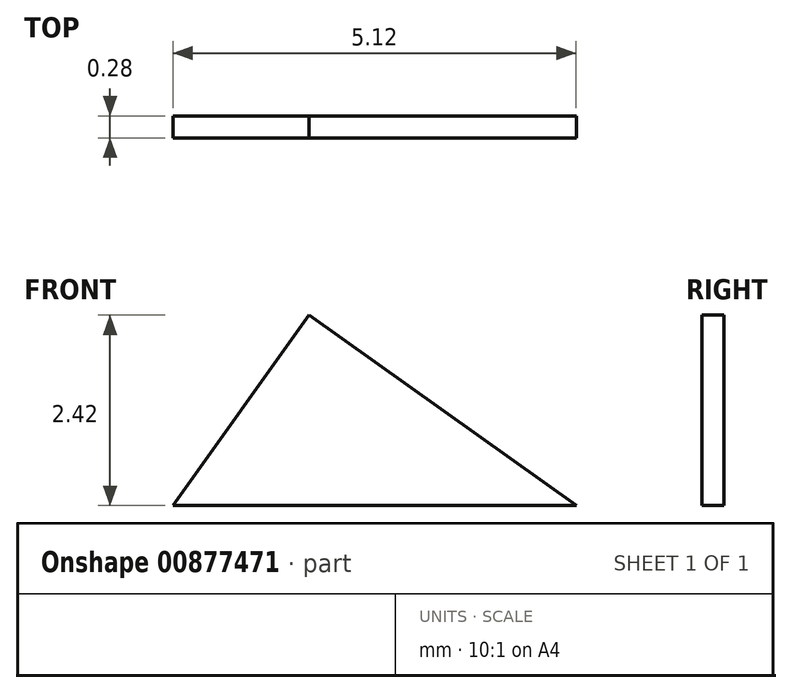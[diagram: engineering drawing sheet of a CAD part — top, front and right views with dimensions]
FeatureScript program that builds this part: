
annotation { "Feature Type Name" : "Feature", "Feature Type Description" : "" }
export const myFeature = defineFeature(function(context is Context, id is Id, definition is map)
    precondition{}
    {
        {
            var Q0;
            Q0=qCreatedBy(makeId("Front.planeOp"),FACE);
            var sketch = newSketch(context, id + "F0", { "sketchPlane" : qUnion([Q0])});
            skLineSegment(sketch, "E0", {"start": v(-6.23, 0) * mm, "end": v(-1.1, 0) * mm});
            skLineSegment(sketch, "E1", {"start": v(-1.1, 0) * mm, "end": v(-4.5, 2.42) * mm});
            skLineSegment(sketch, "E2", {"start": v(-4.5, 2.42) * mm, "end": v(-6.23, 0) * mm});
            skSolve(sketch);
        }
        {
            var Q0;
            Q0=makeQuery(id+"F0.imprint","IMPRINT",FACE,{"disambiguationData":[TD([[makeQuery(id+"F0.imprint","IMPRINT",EDGE,{"derivedFrom":sQuery(id+"F0.wireOp",EDGE,"E0")}),1.0]])]});
            extrude(context, id + "F1", {"entities" : qUnion([Q0]), "depth" : 0.28 * mm, "offsetDistance" : 25.4 * mm});
        }
    });
